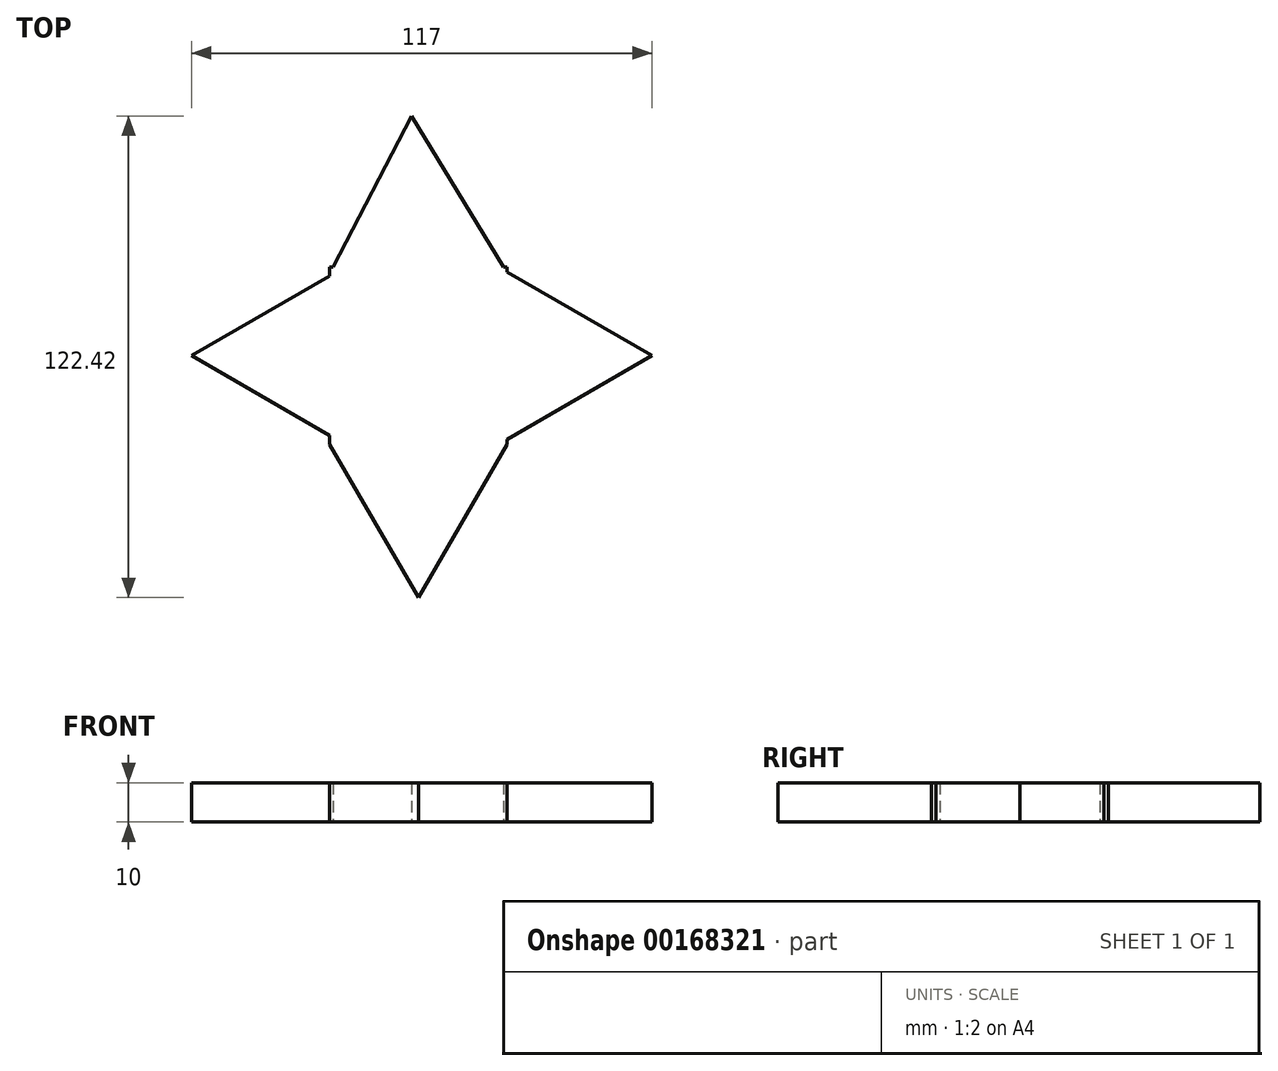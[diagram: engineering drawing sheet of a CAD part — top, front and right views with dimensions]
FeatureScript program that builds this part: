
annotation { "Feature Type Name" : "Feature", "Feature Type Description" : "" }
export const myFeature = defineFeature(function(context is Context, id is Id, definition is map)
    precondition{}
    {
        {
            var Q0;
            Q0=qCreatedBy(makeId("Top.planeOp"),FACE);
            var sketch = newSketch(context, id + "F0", { "sketchPlane" : qUnion([Q0])});
            skLineSegment(sketch, "E0.bottom", {"start": v(-22.5, 22.5) * mm, "end": v(22.5, 22.5) * mm});
            skLineSegment(sketch, "E0.top", {"start": v(-22.5, -22.5) * mm, "end": v(22.5, -22.5) * mm});
            skLineSegment(sketch, "E0.left", {"start": v(-22.5, 22.5) * mm, "end": v(-22.5, -22.5) * mm});
            skLineSegment(sketch, "E0.right", {"start": v(22.5, 22.5) * mm, "end": v(22.5, -22.5) * mm});
            skPoint(sketch, "E0.middle", {"position": v(0, 0) * mm});
            skSolve(sketch);
        }
        {
            var Q0;
            Q0 = qSketchRegion(id + "F0", true);
            extrude(context, id + "F1", {"entities" : qUnion([Q0]), "depth" : 10 * mm});
        }
        {
            var Q0;
            Q0=qCreatedBy(makeId("Top.planeOp"),FACE);
            var sketch = newSketch(context, id + "F2", { "sketchPlane" : qUnion([Q0])});
            skLineSegment(sketch, "E1.0", {"start": v(21.65, 22.5) * mm, "end": v(-21.65, 22.5) * mm});
            skLineSegment(sketch, "E1.1", {"start": v(-21.65, 22.5) * mm, "end": v(-1.73, 60.95) * mm});
            skLineSegment(sketch, "E1.2", {"start": v(-1.73, 60.95) * mm, "end": v(21.65, 22.5) * mm});
            skSolve(sketch);
        }
        {
            var Q0;
            Q0 = qSketchRegion(id + "F2", true);
            extrude(context, id + "F3", {"entities" : qUnion([Q0]), "operationType" : NewBodyOperationType.ADD, "depth" : 10 * mm});
        }
        {
            var Q0;
            Q0=qCreatedBy(makeId("Top.planeOp"),FACE);
            var sketch = newSketch(context, id + "F4", { "sketchPlane" : qUnion([Q0])});
            skCircle(sketch, "E2.cCircle", {"center": v(34.8, 0) * mm, "radius": 24.59 * mm, "construction": true});
            skLineSegment(sketch, "E2.0", {"start": v(59.38, 0) * mm, "end": v(22.5, -21.3) * mm});
            skLineSegment(sketch, "E2.1", {"start": v(22.5, -21.3) * mm, "end": v(22.5, 21.3) * mm});
            skLineSegment(sketch, "E2.2", {"start": v(22.5, 21.3) * mm, "end": v(59.38, 0) * mm});
            skSolve(sketch);
        }
        {
            var Q0;
            Q0 = qSketchRegion(id + "F4", true);
            extrude(context, id + "F5", {"entities" : qUnion([Q0]), "operationType" : NewBodyOperationType.ADD, "depth" : 10 * mm});
        }
        {
            var Q0;
            Q0=qCreatedBy(makeId("Top.planeOp"),FACE);
            var sketch = newSketch(context, id + "F6", { "sketchPlane" : qUnion([Q0])});
            skCircle(sketch, "E3.cCircle", {"center": v(0, -35.5) * mm, "radius": 25.98 * mm, "construction": true});
            skLineSegment(sketch, "E3.0", {"start": v(0, -61.47) * mm, "end": v(-22.5, -22.5) * mm});
            skLineSegment(sketch, "E3.1", {"start": v(-22.5, -22.5) * mm, "end": v(22.5, -22.5) * mm});
            skLineSegment(sketch, "E3.2", {"start": v(22.5, -22.5) * mm, "end": v(0, -61.47) * mm});
            skSolve(sketch);
        }
        {
            var Q0;
            Q0 = qSketchRegion(id + "F6", true);
            extrude(context, id + "F7", {"entities" : qUnion([Q0]), "operationType" : NewBodyOperationType.ADD, "depth" : 10 * mm});
        }
        {
            var Q0;
            Q0=qCreatedBy(makeId("Top.planeOp"),FACE);
            var sketch = newSketch(context, id + "F8", { "sketchPlane" : qUnion([Q0])});
            skCircle(sketch, "E4.cCircle", {"center": v(-34.2, 0) * mm, "radius": 23.42 * mm, "construction": true});
            skLineSegment(sketch, "E4.0", {"start": v(-57.62, 0) * mm, "end": v(-22.5, 20.28) * mm});
            skLineSegment(sketch, "E4.1", {"start": v(-22.5, 20.28) * mm, "end": v(-22.5, -20.28) * mm});
            skLineSegment(sketch, "E4.2", {"start": v(-22.5, -20.28) * mm, "end": v(-57.62, 0) * mm});
            skSolve(sketch);
        }
        {
            var Q0;
            Q0 = qSketchRegion(id + "F8", true);
            extrude(context, id + "F9", {"entities" : qUnion([Q0]), "operationType" : NewBodyOperationType.ADD, "depth" : 10 * mm});
        }
    });
